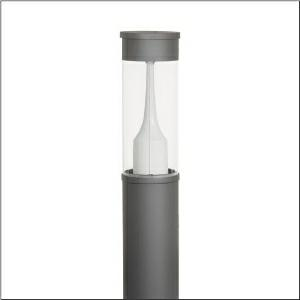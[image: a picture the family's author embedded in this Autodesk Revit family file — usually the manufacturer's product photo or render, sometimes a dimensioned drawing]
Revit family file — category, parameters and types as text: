
# Revit family: city-light_400_iq___p1_0a_5xa5305ff14h_0bc5
name_source: partatom
category: Lighting Fixtures
units: mm (PartAtom-declared; Revit-internal decimal feet)

## family parameters
Cut with Voids When Loaded = No
Host = Face
Light Source = No
Part Type = Normal
Room Calculation Point = No
Round Connector Dimension = Use Diameter
Shared = No

## types (1)
- --- (1 x LED, 1510 lm, 10.5 W, 3000K)
    Apparent Load = 11 VA
    CIE Flux Codes = 32 61 90 93 100
    Color Rendering = 70
    Color Temperature = 3000K
    Default Elevation = 1800 mm
    Description = City-Light 400, light pillar, Module 540 iQ-SR, primary light control with 3 zone facetted reflector, of plastic, silver coated, highly specular, structured, primary optical cover: cover, of PMMA, transparent, light distribution: P1.0a, primary light characteristic: strongly asymmetric, LED, High Power LED, rated luminous flux: 1.510lm, luminous efficacy: 144lm/W, light colour: 730, colour temperature: 3000K, control gear: ECG iQ, control: Auto-Match, Temp-Guard, Lumen-Switch, Night-Set, Smart-Wire, Light-Fading, Desk-Remote (wireless, voltage-free reading and setting of iQ features in the workshop via application-optimized NFC function/RFID function), optimised constant luminous flux control (CLO 2.0), Street-Remote, presetting dimming logarithmic, with terminal, 6-pole, max. 2.5mm², mains connection: 220..240V, AC, 50/60Hz, start of lifetime: 11W, end of lifetime: 11W, reduction: 5W, luminaire housing, cylindrical, of extruded aluminium section, coated, Siteco® metallic grey (DB 702S), length: 4.694mm, diameter: 200mm, Module 540 iQ-SR, traffic white (RAL 9016), equipment: standard, protection rating (complete): IP65, insulation class (complete): insulation class II (safety insulation), certification: CE, ENEC, VDE, packaging unit: 1 piece

Light Distribution: P1.0a
    Height = 500 mm
    Lamp = 1 x LED
    Lamp Light Flux = 1510 lm
    Lamp Power = 10.5 W
    Lamp count = 1
    Length = 200 mm  [stored 0.656168 ft]
    Luminous efficacy = 144 lm/W
    Manufacturer = Siteco
    ModVariant = No
    Model = 5XA5305FF14H
    Mounting Place = Floor
    Mounting Type = Freestanding
    Number of Poles = 1
    OnlyDefault = Yes
    Power Factor = 1
    Product Name = City-Light 400 iQ | P1.0a
    Product group = light pillar | freestanding
    ProductGroupID = 1301
    Protection Class = Protection class II
    Protection Degree = IP 65
    RLX_Detail_Level = 1
    RlxData = <blob elided: 75337 chars, md5=ed73ef31>
    Socket = socket
    Standby Power = 0 W
    System Light Flux = 1510 lm
    System Power = 11 W
    Type Comments = factory setting: luminous flux: 100 % | dim-lin: 254 | 419 mA
    Type Image = l_1006914.jpg
    URL = http://relux.com
    VarID = @adj_070645
    Voltage = 0 V
    Weight = 0.00 kg
    Width = 0 mm  [stored 0 ft]

note: [stored X ft] marks values corroborated as IEEE doubles in the binary element streams (Revit-internal decimal feet)

## geometry (parser evidence)
native form markers: Blend x4, Sweep x11
no freeform markers — native parametric forms only
